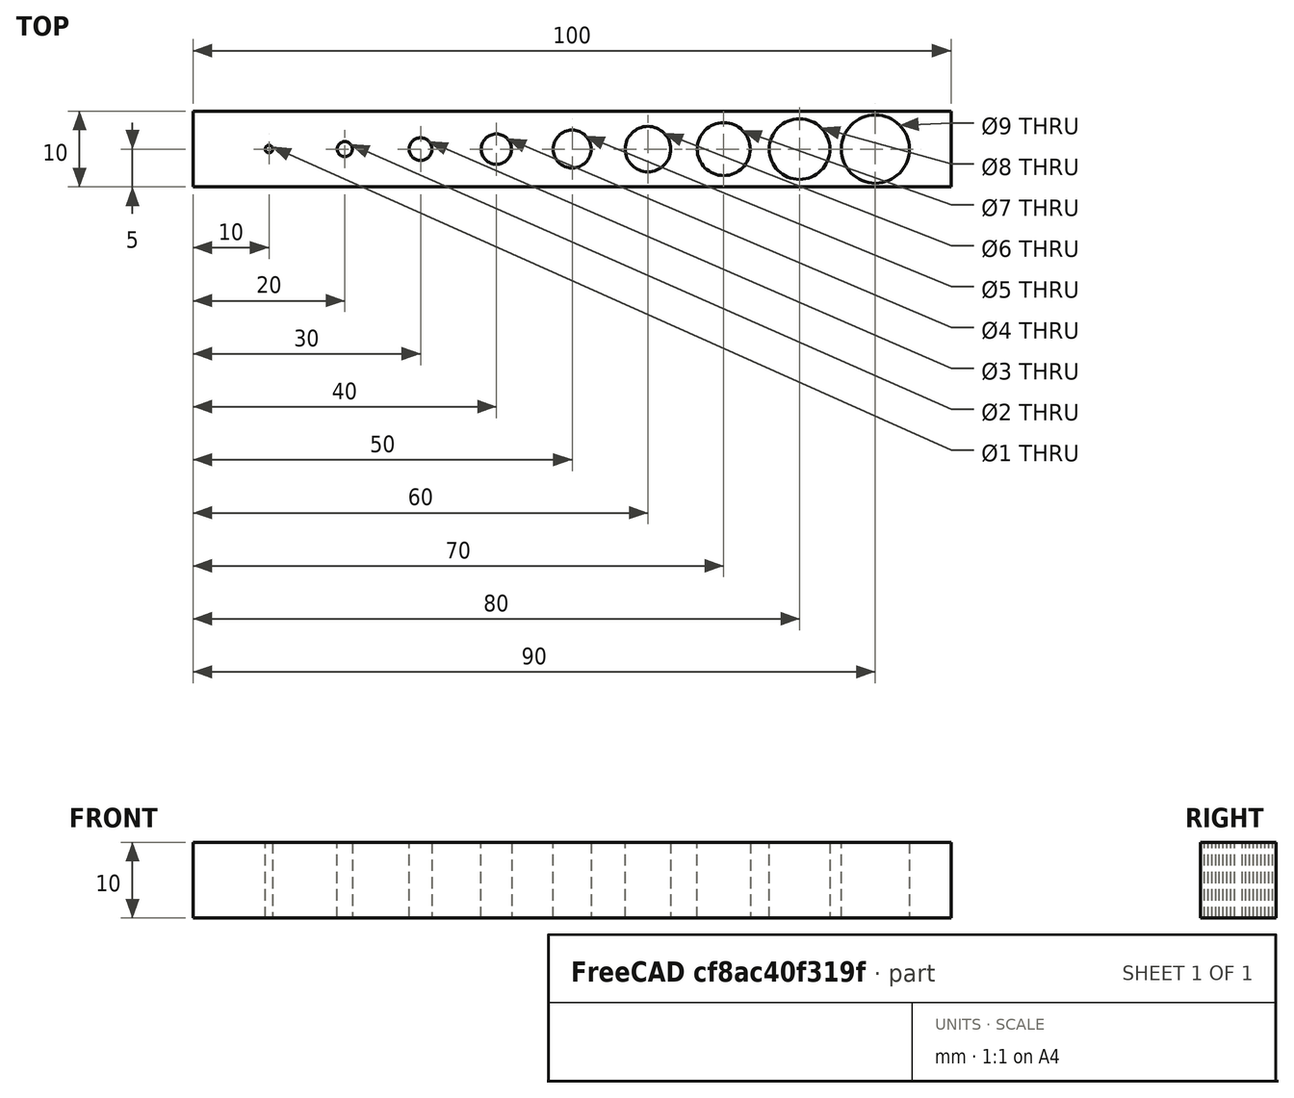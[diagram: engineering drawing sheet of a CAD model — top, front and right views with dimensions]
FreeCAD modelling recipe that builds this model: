
FCSTD DOCUMENT  (FreeCAD 0.19R17639 +1 (Git))
Label: test_holes00
License: All rights reserved
LicenseURL: http://en.wikipedia.org/wiki/All_rights_reserved
objects: Sketcher::SketchObject×1, PartDesign::Pad×1, PartDesign::Body×1
note: 4 computed .brp shape members not serialized (recipe doc carries the construction recipe); baked Part::Feature solids carry a one-line shape summary decoded from their .brp

FEATURE [Sketcher::SketchObject] Sketch
  MapMode = 5
  Support = -> [XY_Plane]
  sketch-geometry (13):
    g0: LineSegment StartX=0 StartY=5 StartZ=0 EndX=100 EndY=5 EndZ=0
    g1: LineSegment StartX=100 StartY=5 StartZ=0 EndX=100 EndY=-5 EndZ=0
    g2: LineSegment StartX=100 StartY=-5 StartZ=0 EndX=0 EndY=-5 EndZ=0
    g3: LineSegment StartX=0 StartY=-5 StartZ=0 EndX=0 EndY=5 EndZ=0
    g4: Circle CenterX=20 CenterY=0 CenterZ=0 NormalX=0 NormalY=0 NormalZ=1 AngleXU=0 Radius=1
    g5: Circle CenterX=40 CenterY=0 CenterZ=0 NormalX=0 NormalY=0 NormalZ=1 AngleXU=0 Radius=2
    g6: Circle CenterX=60 CenterY=0 CenterZ=0 NormalX=0 NormalY=0 NormalZ=1 AngleXU=0 Radius=3
    g7: Circle CenterX=80 CenterY=0 CenterZ=0 NormalX=0 NormalY=0 NormalZ=1 AngleXU=0 Radius=4
    g8: Circle CenterX=10 CenterY=0 CenterZ=0 NormalX=0 NormalY=0 NormalZ=1 AngleXU=0 Radius=0.5
    g9: Circle CenterX=30 CenterY=0 CenterZ=0 NormalX=0 NormalY=0 NormalZ=1 AngleXU=0 Radius=1.5
    g10: Circle CenterX=50 CenterY=0 CenterZ=0 NormalX=0 NormalY=0 NormalZ=1 AngleXU=0 Radius=2.5
    g11: Circle CenterX=70 CenterY=0 CenterZ=0 NormalX=0 NormalY=0 NormalZ=1 AngleXU=0 Radius=3.5
    g12: Circle CenterX=90 CenterY=0 CenterZ=0 NormalX=0 NormalY=0 NormalZ=1 AngleXU=0 Radius=4.5
  constraints (38):
    c: Coincident(g0,g1)
    c: Coincident(g1,g2)
    c: Coincident(g2,g3)
    c: Coincident(g3,g0)
    c: Horizontal(g0)
    c: Horizontal(g2)
    c: Vertical(g1)
    c: Vertical(g3)
    c: Diameter(g4) = 2
    c: Diameter(g5) = 4
    c: PointOnObject(g4,g-1)
    c: PointOnObject(g5,g-1)
    c: DistanceX(g5) = 40
    c: DistanceX(g4) = 20
    c: Diameter(g6) = 6
    c: DistanceX(g6) = 60
    c: Diameter(g7) = 8
    c: DistanceX(g7) = 80
    c: Symmetric(g0,g2,g-1)
    c: DistanceX(g0) = 100
    c: PointOnObject(g7,g-1)
    c: PointOnObject(g6,g-1)
    c: DistanceY(g1,g1) = 10
    c: PointOnObject(g8,g-1)
    c: PointOnObject(g9,g-1)
    c: PointOnObject(g10,g-1)
    c: PointOnObject(g11,g-1)
    c: PointOnObject(g12,g-1)
    c: DistanceX(g8) = 10
    c: DistanceX(g9) = 30
    c: DistanceX(g10) = 50
    c: DistanceX(g11) = 70
    c: DistanceX(g12) = 90
    c: Diameter(g12) = 9
    c: Diameter(g11) = 7
    c: Diameter(g10) = 5
    c: Diameter(g9) = 3
    c: Diameter(g8) = 1
FEATURE [PartDesign::Pad] Pad
  Length = 10
  Length2 = 100
  Profile = -> Sketch
  Reversed = true
  Type = 0
FEATURE [PartDesign::Body] Body
  Group = -> [Sketch,Pad]
  Origin = -> Origin
  Tip = -> Pad
